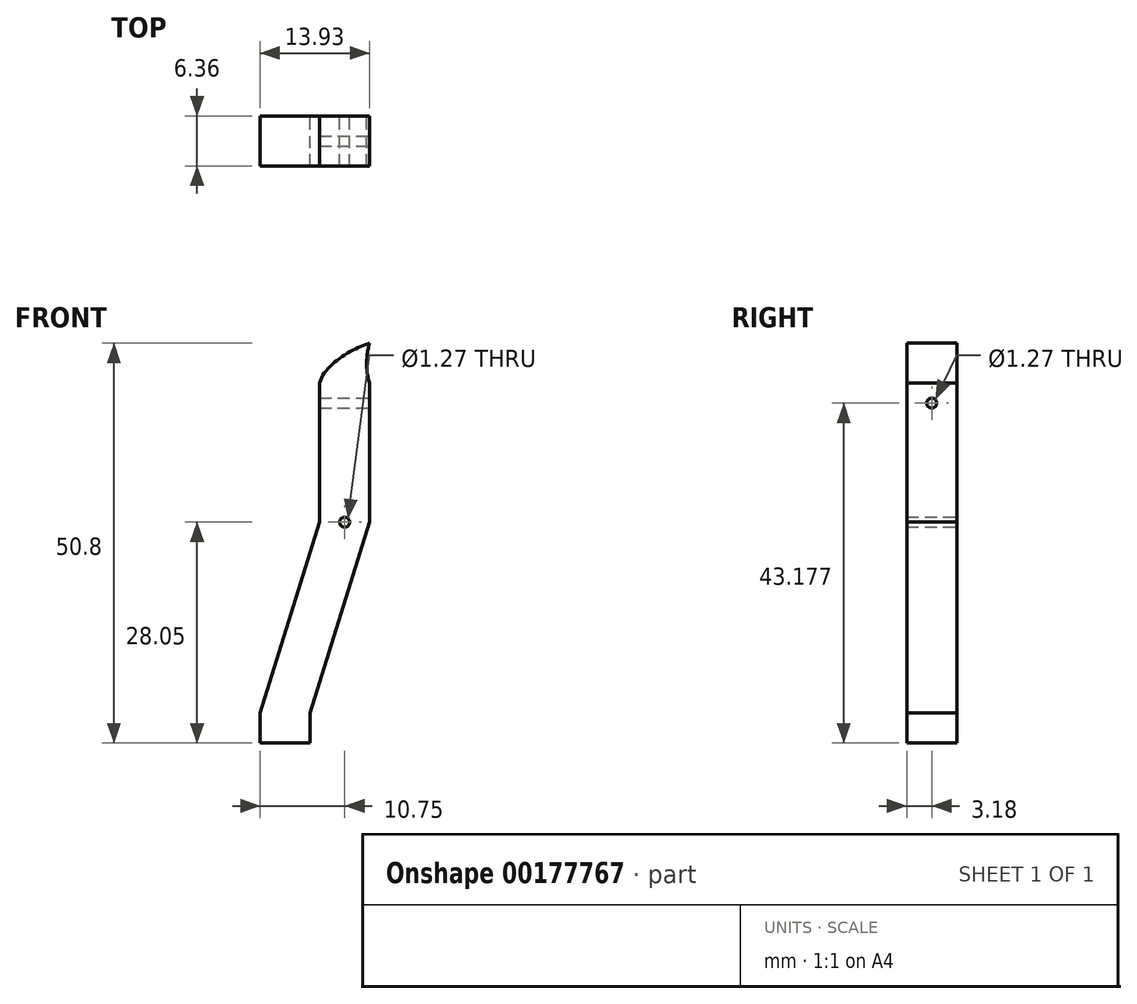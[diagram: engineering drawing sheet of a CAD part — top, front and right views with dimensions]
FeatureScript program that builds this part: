
annotation { "Feature Type Name" : "Feature", "Feature Type Description" : "" }
export const myFeature = defineFeature(function(context is Context, id is Id, definition is map)
    precondition{}
    {
        {
            var Q0;
            Q0=qCreatedBy(makeId("Front.planeOp"),FACE);
            var sketch = newSketch(context, id + "F0", { "sketchPlane" : qUnion([Q0])});
            skLineSegment(sketch, "E0.bottom", {"start": v(-3.17, 17.67) * mm, "end": v(3.17, 17.67) * mm});
            skLineSegment(sketch, "E0.left", {"start": v(-3.17, 17.67) * mm, "end": v(-3.17, 0) * mm});
            skLineSegment(sketch, "E0.right", {"start": v(3.17, 17.67) * mm, "end": v(3.17, 0) * mm});
            skFitSpline(sketch, "E1", {"points": [v(-3.18, 17.67) * mm, v(3.18, 22.75) * mm], "startDerivative": vector(1.8, 7.54) * mm, "endDerivative": vector(5.73, 1.8) * mm});
            skFitSpline(sketch, "E2", {"points": [v(3.18, 17.67) * mm, v(3.18, 22.75) * mm], "startDerivative": vector(-1.64, 4.51) * mm, "endDerivative": vector(1.33, 4.33) * mm});
            skLineSegment(sketch, "E3", {"start": v(-3.17, 0) * mm, "end": v(-10.75, -24.24) * mm});
            skLineSegment(sketch, "E4.0", {"start": v(3.17, 0) * mm, "end": v(-4.4, -24.24) * mm});
            skLineSegment(sketch, "E5", {"start": v(-10.75, -24.24) * mm, "end": v(-4.4, -24.24) * mm});
            skLineSegment(sketch, "E6", {"start": v(-10.75, -24.24) * mm, "end": v(-10.75, -28.05) * mm});
            skLineSegment(sketch, "E7", {"start": v(-10.75, -28.05) * mm, "end": v(-4.4, -28.05) * mm});
            skLineSegment(sketch, "E8", {"start": v(-4.4, -28.05) * mm, "end": v(-4.4, -26.15) * mm});
            skLineSegment(sketch, "E9", {"start": v(-4.4, -26.15) * mm, "end": v(-4.4, -26.15) * mm});
            skLineSegment(sketch, "E10", {"start": v(-4.4, -26.15) * mm, "end": v(-4.4, -24.24) * mm});
            skCircle(sketch, "E11", {"center": v(0, 0) * mm, "radius": 0.64 * mm});
            skSolve(sketch);
        }
        {
            var Q0;
            Q0 = qSketchRegion(id + "F0", true);
            extrude(context, id + "F1", {"entities" : qUnion([Q0]), "endBound" : BoundingType.SYMMETRIC, "depth" : 6.35 * mm});
        }
        {
            var Q0;
            Q0=makeQuery(id+"F1.opExtrude","SWEPT_FACE",FACE,{"disambiguationData":[OSD([sQuery(id+"F0.wireOp",EDGE,"E0.right")])]});
            var sketch = newSketch(context, id + "F2", { "sketchPlane" : qUnion([Q0])});
            skCircle(sketch, "E12", {"center": v(0, 15.13) * mm, "radius": 0.64 * mm});
            skSolve(sketch);
        }
        {
            var Q0;
            Q0=sQuery(id+"F2.wireOp",VERTEX,"E12.center");
            var Q1;
            Q1=makeQuery(id+"F1.opExtrude","SWEPT_BODY",BODY,{"disambiguationData":[OSD([sQuery(id+"F0.wireOp",EDGE,"E0.left"),sQuery(id+"F0.wireOp",EDGE,"E0.right"),sQuery(id+"F0.wireOp",EDGE,"E1"),sQuery(id+"F0.wireOp",EDGE,"E2"),sQuery(id+"F0.wireOp",EDGE,"E3"),sQuery(id+"F0.wireOp",EDGE,"E4.0"),sQuery(id+"F0.wireOp",EDGE,"E5"),sQuery(id+"F0.wireOp",EDGE,"E6"),sQuery(id+"F0.wireOp",EDGE,"E7"),sQuery(id+"F0.wireOp",EDGE,"E8"),sQuery(id+"F0.wireOp",EDGE,"E9"),sQuery(id+"F0.wireOp",EDGE,"E10"),sQuery(id+"F0.wireOp",EDGE,"E11")])]});
            hole(context, id + "F3", {"style" : HoleStyle.SIMPLE, "endStyle" : HoleEndStyle.THROUGH, "holeDiameter" : 1.27 * mm, "locations" : qUnion([Q0]), "scope" : qUnion([Q1]), "isTappedThrough" : true});
        }
    });
